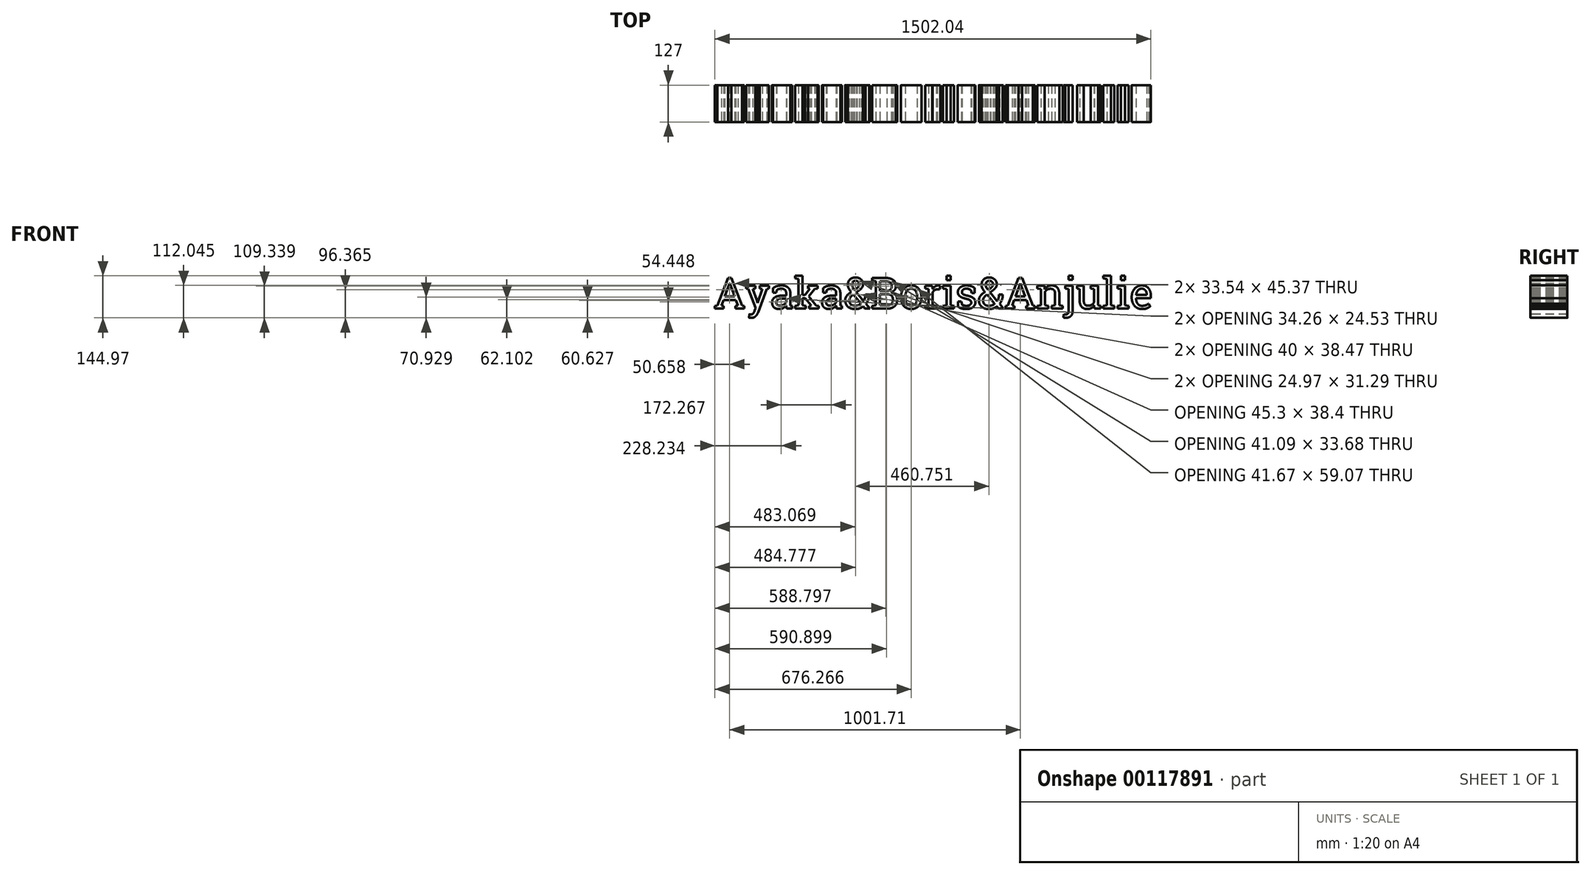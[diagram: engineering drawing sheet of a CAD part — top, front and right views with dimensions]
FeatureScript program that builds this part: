
annotation { "Feature Type Name" : "Feature", "Feature Type Description" : "" }
export const myFeature = defineFeature(function(context is Context, id is Id, definition is map)
    precondition{}
    {
        {
            var Q0;
            Q0=qCreatedBy(makeId("Front.planeOp"),FACE);
            var sketch = newSketch(context, id + "F0", { "sketchPlane" : qUnion([Q0])});
            skText(sketch, "E0", { "text": "Ayaka&Boris&Anjulie", "fontName": "RobotoSlab-Regular.ttf"});
            const initialGuessF0  = {"E0": [-0.1229, -0.06188, 1, 0, 0.10704]};
            skSetInitialGuess(sketch, initialGuessF0);
            skSolve(sketch);
        }
        {
            var Q0;
            Q0 = qSketchRegion(id + "F0", true);
            extrude(context, id + "F1", {"entities" : qUnion([Q0]), "oppositeDirection" : true, "depth" : 127 * mm});
        }
    });
